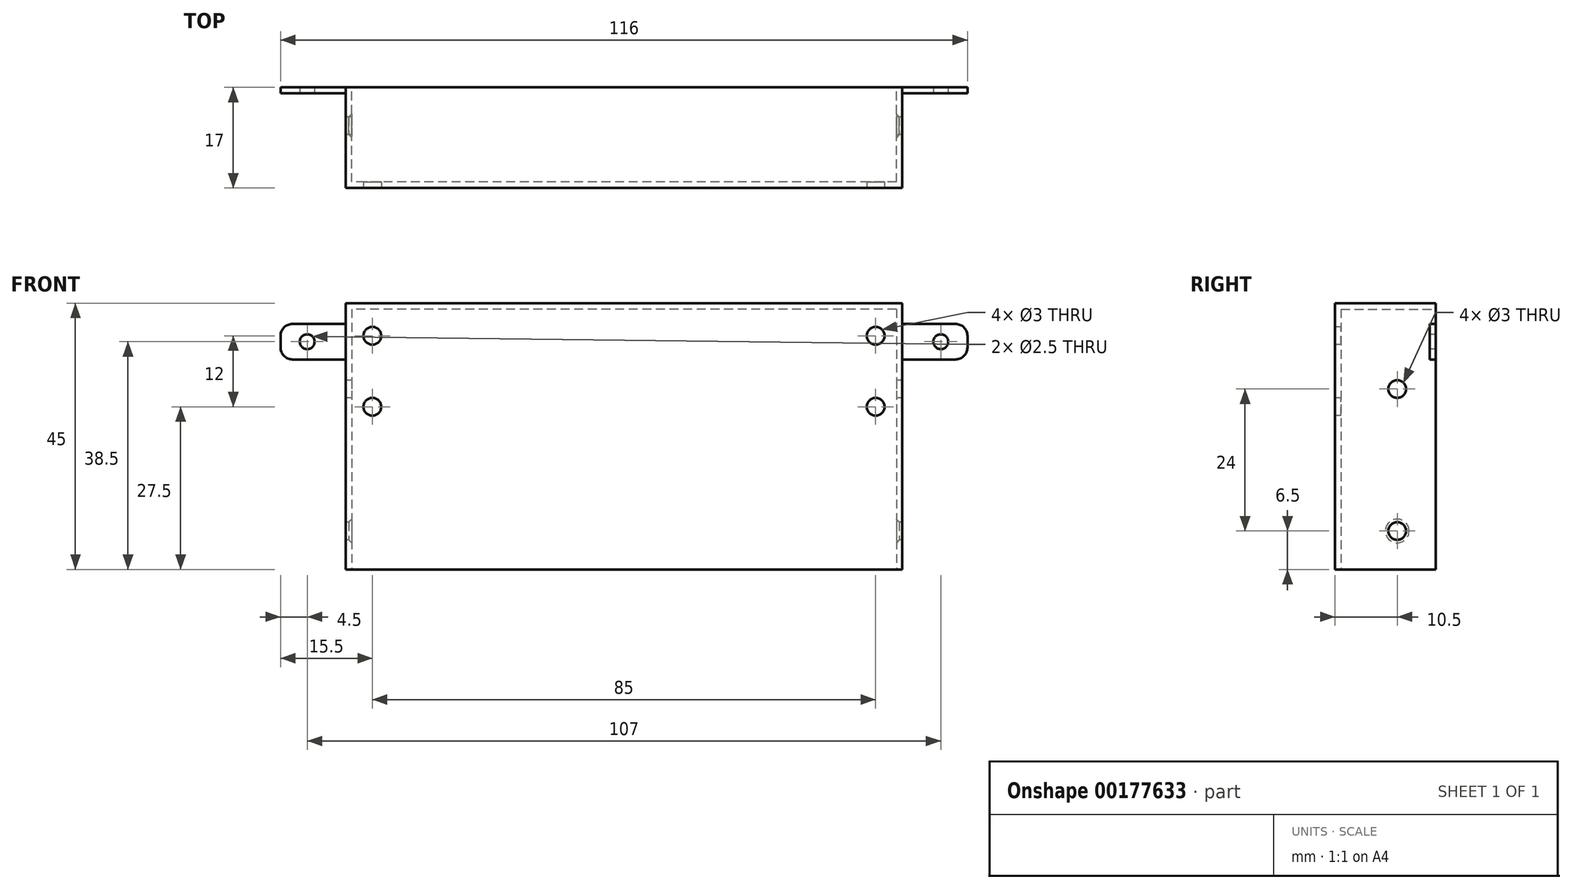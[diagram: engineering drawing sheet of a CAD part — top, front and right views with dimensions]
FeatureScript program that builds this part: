
annotation { "Feature Type Name" : "Feature", "Feature Type Description" : "" }
export const myFeature = defineFeature(function(context is Context, id is Id, definition is map)
    precondition{}
    {
        {
            var Q0;
            Q0=qCreatedBy(makeId("Front.planeOp"),FACE);
            var sketch = newSketch(context, id + "F0", { "sketchPlane" : qUnion([Q0])});
            skLineSegment(sketch, "E0.bottom", {"start": v(47, 22.5) * mm, "end": v(-47, 22.5) * mm});
            skLineSegment(sketch, "E0.top", {"start": v(47, -22.5) * mm, "end": v(-47, -22.5) * mm});
            skLineSegment(sketch, "E0.left", {"start": v(47, 22.5) * mm, "end": v(47, -22.5) * mm});
            skLineSegment(sketch, "E0.right", {"start": v(-47, 22.5) * mm, "end": v(-47, -22.5) * mm});
            skPoint(sketch, "E0.middle", {"position": v(0, 0) * mm});
            skSolve(sketch);
        }
        {
            var Q0;
            Q0 = qSketchRegion(id + "F0", true);
            extrude(context, id + "F1", {"entities" : qUnion([Q0]), "depth" : 1 * mm});
        }
        {
            var Q0;
            Q0=makeQuery(id+"F1.opExtrude","CAP_FACE",FACE,{"disambiguationData":[OSD([sQuery(id+"F0.wireOp",EDGE,"E0.bottom"),sQuery(id+"F0.wireOp",EDGE,"E0.top"),sQuery(id+"F0.wireOp",EDGE,"E0.left"),sQuery(id+"F0.wireOp",EDGE,"E0.right")])],"isStart":true});
            var sketch = newSketch(context, id + "F2", { "sketchPlane" : qUnion([Q0])});
            skLineSegment(sketch, "E1.bottom", {"start": v(-47, 22.5) * mm, "end": v(-46, 22.5) * mm});
            skLineSegment(sketch, "E1.top", {"start": v(-47, -22.5) * mm, "end": v(-46, -22.5) * mm});
            skLineSegment(sketch, "E1.left", {"start": v(-47, 22.5) * mm, "end": v(-47, -22.5) * mm});
            skLineSegment(sketch, "E1.right", {"start": v(-46, 22.5) * mm, "end": v(-46, -22.5) * mm});
            skLineSegment(sketch, "E2.bottom", {"start": v(47, 22.5) * mm, "end": v(46, 22.5) * mm});
            skLineSegment(sketch, "E2.top", {"start": v(47, -22.5) * mm, "end": v(46, -22.5) * mm});
            skLineSegment(sketch, "E2.left", {"start": v(47, 22.5) * mm, "end": v(47, -22.5) * mm});
            skLineSegment(sketch, "E2.right", {"start": v(46, 22.5) * mm, "end": v(46, -22.5) * mm});
            skSolve(sketch);
        }
        {
            var Q0;
            Q0 = qSketchRegion(id + "F2", true);
            extrude(context, id + "F3", {"entities" : qUnion([Q0]), "operationType" : NewBodyOperationType.ADD, "depth" : 16 * mm});
        }
        {
            var Q0;
            Q0=makeQuery(id+"F3.boolean.opBoolean","MERGE",FACE,{"derivedFrom":[makeQuery(id+"F1.opExtrude","SWEPT_FACE",FACE,{"disambiguationData":[OSD([sQuery(id+"F0.wireOp",EDGE,"E0.bottom")])]}),makeQuery(id+"F3.opExtrude","SWEPT_FACE",FACE,{"disambiguationData":[OSD([sQuery(id+"F2.wireOp",EDGE,"E1.bottom")])]}),makeQuery(id+"F3.opExtrude","SWEPT_FACE",FACE,{"disambiguationData":[OSD([sQuery(id+"F2.wireOp",EDGE,"E2.bottom")])]})]});
            var sketch = newSketch(context, id + "F4", { "sketchPlane" : qUnion([Q0])});
            skLineSegment(sketch, "E3.bottom", {"start": v(-47, -1) * mm, "end": v(47, -1) * mm});
            skLineSegment(sketch, "E3.top", {"start": v(-47, 16) * mm, "end": v(47, 16) * mm});
            skLineSegment(sketch, "E3.left", {"start": v(-47, -1) * mm, "end": v(-47, 16) * mm});
            skLineSegment(sketch, "E3.right", {"start": v(47, -1) * mm, "end": v(47, 16) * mm});
            skSolve(sketch);
        }
        {
            var Q0;
            Q0 = qSketchRegion(id + "F4", true);
            extrude(context, id + "F5", {"entities" : qUnion([Q0]), "operationType" : NewBodyOperationType.ADD, "oppositeDirection" : true, "depth" : 1 * mm});
        }
        {
            var Q0;
            Q0=makeQuery(id+"F3.boolean.opBoolean","MERGE",FACE,{"derivedFrom":[makeQuery(id+"F1.opExtrude","SWEPT_FACE",FACE,{"disambiguationData":[OSD([sQuery(id+"F0.wireOp",EDGE,"E0.left")])]}),makeQuery(id+"F3.opExtrude","SWEPT_FACE",FACE,{"disambiguationData":[OSD([sQuery(id+"F2.wireOp",EDGE,"E1.left")])]})]});
            var sketch = newSketch(context, id + "F6", { "sketchPlane" : qUnion([Q0])});
            skLineSegment(sketch, "E4", {"start": v(16, 22.5) * mm, "end": v(16, -22.5) * mm, "construction": true});
            skLineSegment(sketch, "E5", {"start": v(16, -22.5) * mm, "end": v(-1, -22.5) * mm, "construction": true});
            skLineSegment(sketch, "E6", {"start": v(-1, -22.5) * mm, "end": v(-1, 0) * mm, "construction": true});
            skLineSegment(sketch, "E7", {"start": v(-1, 0) * mm, "end": v(44.18, 0) * mm, "construction": true});
            skLineSegment(sketch, "E8.bottom", {"start": v(16, 19) * mm, "end": v(15, 19) * mm});
            skLineSegment(sketch, "E8.top", {"start": v(16, 13) * mm, "end": v(15, 13) * mm});
            skLineSegment(sketch, "E8.left", {"start": v(16, 19) * mm, "end": v(16, 13) * mm});
            skLineSegment(sketch, "E8.right", {"start": v(15, 19) * mm, "end": v(15, 13) * mm});
            skLineSegment(sketch, "E9.bottom", {"start": v(16, -13) * mm, "end": v(15, -13) * mm});
            skLineSegment(sketch, "E9.top", {"start": v(16, -19) * mm, "end": v(15, -19) * mm});
            skLineSegment(sketch, "E9.left", {"start": v(16, -13) * mm, "end": v(16, -19) * mm});
            skLineSegment(sketch, "E9.right", {"start": v(15, -13) * mm, "end": v(15, -19) * mm});
            skSolve(sketch);
        }
        {
            var Q0;
            Q0 = qSketchRegion(id + "F6", true);
            extrude(context, id + "F7", {"entities" : qUnion([Q0]), "operationType" : NewBodyOperationType.ADD, "depth" : 11 * mm});
        }
        {
            var Q0;
            Q0=makeQuery(id+"F7.opExtrude","SWEPT_FACE",FACE,{"disambiguationData":[OSD([sQuery(id+"F6.wireOp",EDGE,"E8.right")])]});
            var sketch = newSketch(context, id + "F8", { "sketchPlane" : qUnion([Q0])});
            skCircle(sketch, "E10", {"center": v(53.5, 16) * mm, "radius": 1.25 * mm});
            skCircle(sketch, "E11", {"center": v(53.5, -16) * mm, "radius": 1.5 * mm});
            skSolve(sketch);
        }
        {
            var Q0;
            Q0 = qSketchRegion(id + "F8", true);
            extrude(context, id + "F9", {"entities" : qUnion([Q0]), "operationType" : NewBodyOperationType.REMOVE, "oppositeDirection" : true, "depth" : 25 * mm});
        }
        {
            var Q0;
            Q0=makeQuery(id+"F7.opExtrude","CAP_EDGE",EDGE,{"disambiguationData":[OSD([sQuery(id+"F6.wireOp",EDGE,"E9.top")])],"isStart":false});
            var Q1;
            Q1=makeQuery(id+"F7.opExtrude","CAP_EDGE",EDGE,{"disambiguationData":[OSD([sQuery(id+"F6.wireOp",EDGE,"E9.bottom")])],"isStart":false});
            var Q2;
            Q2=makeQuery(id+"F7.opExtrude","CAP_EDGE",EDGE,{"disambiguationData":[OSD([sQuery(id+"F6.wireOp",EDGE,"E8.bottom")])],"isStart":false});
            var Q3;
            Q3=makeQuery(id+"F7.opExtrude","CAP_EDGE",EDGE,{"disambiguationData":[OSD([sQuery(id+"F6.wireOp",EDGE,"E8.top")])],"isStart":false});
            var Q4;
            Q4=makeQuery(id+"F7.opExtrude","CAP_EDGE",EDGE,{"disambiguationData":[OSD([sQuery(id+"F6.wireOp",EDGE,"E9.right")])],"isStart":true});
            var Q5;
            Q5=makeQuery(id+"F7.opExtrude","CAP_EDGE",EDGE,{"disambiguationData":[OSD([sQuery(id+"F6.wireOp",EDGE,"E8.right")])],"isStart":true});
            fillet(context, id + "F10", {"entities" : qUnion([Q0, Q1, Q2, Q3, Q4, Q5]), "radius" : 2 * mm, "tangentPropagation" : true, "allowEdgeOverflow" : false});
        }
        {
            var Q0;
            Q0=makeQuery(id+"F1.opExtrude","SWEPT_BODY",BODY,{"disambiguationData":[OSD([sQuery(id+"F0.wireOp",EDGE,"E0.bottom"),sQuery(id+"F0.wireOp",EDGE,"E0.top"),sQuery(id+"F0.wireOp",EDGE,"E0.left"),sQuery(id+"F0.wireOp",EDGE,"E0.right")])]});
            var Q1;
            Q1=qCreatedBy(makeId("Right.planeOp"),FACE);
            mirror(context, id + "F11", {"operationType" : NewBodyOperationType.ADD, "entities" : qUnion([Q0]), "mirrorPlane" : qUnion([Q1])});
        }
        {
            var Q0;
            Q0=makeQuery(id+"F1.opExtrude","CAP_FACE",FACE,{"disambiguationData":[OSD([sQuery(id+"F0.wireOp",EDGE,"E0.bottom"),sQuery(id+"F0.wireOp",EDGE,"E0.top"),sQuery(id+"F0.wireOp",EDGE,"E0.left"),sQuery(id+"F0.wireOp",EDGE,"E0.right")])],"isStart":false});
            var sketch = newSketch(context, id + "F12", { "sketchPlane" : qUnion([Q0])});
            skLineSegment(sketch, "E12.bottom", {"start": v(47, -22.5) * mm, "end": v(66.27, -22.5) * mm});
            skLineSegment(sketch, "E12.top", {"start": v(47, -7.64) * mm, "end": v(66.27, -7.64) * mm});
            skLineSegment(sketch, "E12.left", {"start": v(47, -22.5) * mm, "end": v(47, -7.64) * mm});
            skLineSegment(sketch, "E12.right", {"start": v(66.27, -22.5) * mm, "end": v(66.27, -7.64) * mm});
            skLineSegment(sketch, "E13.bottom", {"start": v(-47, -22.5) * mm, "end": v(-63.88, -22.5) * mm});
            skLineSegment(sketch, "E13.top", {"start": v(-47, -7.22) * mm, "end": v(-63.88, -7.22) * mm});
            skLineSegment(sketch, "E13.left", {"start": v(-47, -22.5) * mm, "end": v(-47, -7.22) * mm});
            skLineSegment(sketch, "E13.right", {"start": v(-63.88, -22.5) * mm, "end": v(-63.88, -7.22) * mm});
            skSolve(sketch);
        }
        {
            var Q0;
            Q0 = qSketchRegion(id + "F12", true);
            extrude(context, id + "F13", {"entities" : qUnion([Q0]), "operationType" : NewBodyOperationType.REMOVE, "oppositeDirection" : true, "depth" : 25 * mm});
        }
        {
            var Q0;
            Q0=makeQuery(id+"F13.boolean.opBoolean","MERGE",FACE,{"derivedFrom":[makeQuery(id+"F3.boolean.opBoolean","MERGE",FACE,{"derivedFrom":[makeQuery(id+"F1.opExtrude","SWEPT_FACE",FACE,{"disambiguationData":[OSD([sQuery(id+"F0.wireOp",EDGE,"E0.right")])]}),makeQuery(id+"F3.opExtrude","SWEPT_FACE",FACE,{"disambiguationData":[OSD([sQuery(id+"F2.wireOp",EDGE,"E2.left")])]})]}),makeQuery(id+"F13.opExtrude","SWEPT_FACE",FACE,{"disambiguationData":[OSD([sQuery(id+"F12.wireOp",EDGE,"E13.left")])]})]});
            var sketch = newSketch(context, id + "F14", { "sketchPlane" : qUnion([Q0])});
            skCircle(sketch, "E14", {"center": v(-9.5, -16) * mm, "radius": 1.5 * mm});
            skSolve(sketch);
        }
        {
            var Q0;
            Q0 = qSketchRegion(id + "F14", true);
            extrude(context, id + "F15", {"entities" : qUnion([Q0]), "operationType" : NewBodyOperationType.REMOVE, "oppositeDirection" : true, "depth" : 100 * mm});
        }
        {
            var Q0;
            Q0=makeQuery(id+"F15.boolean.opBoolean","INTERSECT",EDGE,{"derivedFrom":[makeQuery(id+"F3.opExtrude","SWEPT_FACE",FACE,{"disambiguationData":[OSD([sQuery(id+"F2.wireOp",EDGE,"E2.right")])]}),makeQuery(id+"F15.opExtrude","SWEPT_FACE",FACE,{"disambiguationData":[OSD([sQuery(id+"F14.wireOp",EDGE,"E14")])]})]});
            var Q1;
            Q1=makeQuery(id+"F15.boolean.opBoolean","INTERSECT",EDGE,{"derivedFrom":[makeQuery(id+"F3.opExtrude","SWEPT_FACE",FACE,{"disambiguationData":[OSD([sQuery(id+"F2.wireOp",EDGE,"E1.right")])]}),makeQuery(id+"F15.opExtrude","SWEPT_FACE",FACE,{"disambiguationData":[OSD([sQuery(id+"F14.wireOp",EDGE,"E14")])]})]});
            chamfer(context, id + "F16", {"entities" : qUnion([Q0, Q1]), "width" : .5 * mm, "tangentPropagation" : true});
        }
        {
            var Q0;
            Q0=makeQuery(id+"F13.boolean.opBoolean","MERGE",FACE,{"derivedFrom":[makeQuery(id+"F3.boolean.opBoolean","MERGE",FACE,{"derivedFrom":[makeQuery(id+"F1.opExtrude","SWEPT_FACE",FACE,{"disambiguationData":[OSD([sQuery(id+"F0.wireOp",EDGE,"E0.right")])]}),makeQuery(id+"F3.opExtrude","SWEPT_FACE",FACE,{"disambiguationData":[OSD([sQuery(id+"F2.wireOp",EDGE,"E2.left")])]})]}),makeQuery(id+"F13.opExtrude","SWEPT_FACE",FACE,{"disambiguationData":[OSD([sQuery(id+"F12.wireOp",EDGE,"E13.left")])]})]});
            var sketch = newSketch(context, id + "F17", { "sketchPlane" : qUnion([Q0])});
            skCircle(sketch, "E15", {"center": v(-9.5, 8) * mm, "radius": 1.5 * mm});
            skSolve(sketch);
        }
        {
            var Q0;
            Q0 = qSketchRegion(id + "F17", true);
            extrude(context, id + "F18", {"entities" : qUnion([Q0]), "operationType" : NewBodyOperationType.REMOVE, "oppositeDirection" : true, "depth" : 100 * mm});
        }
        {
            var Q0;
            Q0=makeQuery(id+"F1.opExtrude","CAP_FACE",FACE,{"disambiguationData":[OSD([sQuery(id+"F0.wireOp",EDGE,"E0.bottom"),sQuery(id+"F0.wireOp",EDGE,"E0.top"),sQuery(id+"F0.wireOp",EDGE,"E0.left"),sQuery(id+"F0.wireOp",EDGE,"E0.right")])],"isStart":false});
            var sketch = newSketch(context, id + "F19", { "sketchPlane" : qUnion([Q0])});
            skLineSegment(sketch, "E16.bottom", {"start": v(-42.5, -1.5) * mm, "end": v(42.5, -1.5) * mm, "construction": true});
            skLineSegment(sketch, "E16.top", {"start": v(-42.5, 18.5) * mm, "end": v(42.5, 18.5) * mm, "construction": true});
            skLineSegment(sketch, "E16.left", {"start": v(-42.5, -1.5) * mm, "end": v(-42.5, 18.5) * mm, "construction": true});
            skLineSegment(sketch, "E16.right", {"start": v(42.5, -1.5) * mm, "end": v(42.5, 18.5) * mm, "construction": true});
            skPoint(sketch, "E16.middle", {"position": v(0, 8.5) * mm});
            skCircle(sketch, "E17", {"center": v(-42.5, 17) * mm, "radius": 1.5 * mm});
            skCircle(sketch, "E18", {"center": v(42.5, 17) * mm, "radius": 1.5 * mm});
            skCircle(sketch, "E19", {"center": v(-42.5, 5) * mm, "radius": 1.5 * mm});
            skCircle(sketch, "E20", {"center": v(42.5, 5) * mm, "radius": 1.5 * mm});
            skSolve(sketch);
        }
        {
            var Q0;
            Q0 = qSketchRegion(id + "F19", true);
            extrude(context, id + "F20", {"entities" : qUnion([Q0]), "operationType" : NewBodyOperationType.REMOVE, "oppositeDirection" : true, "depth" : 25 * mm});
        }
    });
